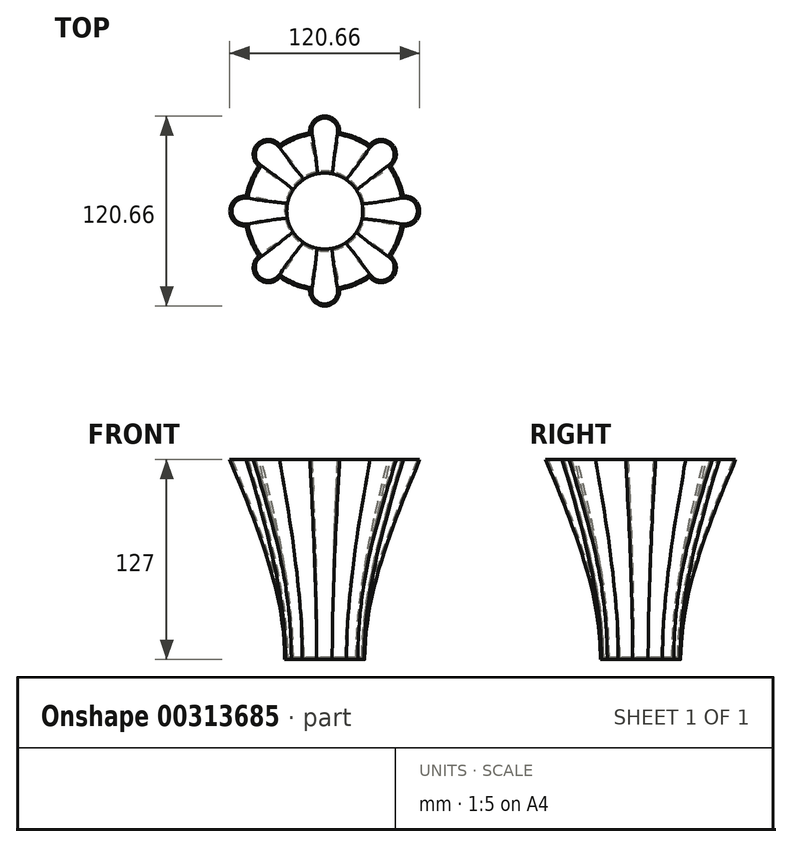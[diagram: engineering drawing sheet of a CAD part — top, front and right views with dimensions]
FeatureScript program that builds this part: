
annotation { "Feature Type Name" : "Feature", "Feature Type Description" : "" }
export const myFeature = defineFeature(function(context is Context, id is Id, definition is map)
    precondition{}
    {
        {
            var Q0;
            Q0=qCreatedBy(makeId("Top.planeOp"),FACE);
            var sketch = newSketch(context, id + "F0", { "sketchPlane" : qUnion([Q0])});
            skCircle(sketch, "E0", {"center": v(0, 0) * mm, "radius": 25.4 * mm});
            skPoint(sketch, "E1", {"position": v(-25.4, 0) * mm});
            skSolve(sketch);
        }
        {
            var Q0;
            Q0=qCreatedBy(makeId("Top.planeOp"),FACE);
            cPlane(context, id + "F1", {"entities" : qUnion([Q0]), "cplaneType" : CPlaneType.OFFSET, "offset" : 127 * mm, "width" : 152.4 * mm, "height" : 152.4 * mm});
        }
        {
            var Q0;
            Q0=qCreatedBy(id+"F1.planeOp",FACE);
            var sketch = newSketch(context, id + "F2", { "sketchPlane" : qUnion([Q0])});
            skArc(sketch, "E2", {"start": v(-42, 28.58) * mm, "mid": v(-46.93, 19.44) * mm, "end": v(-49.9, 9.48) * mm});
            skArc(sketch, "E3", {"start": v(49.9, -9.48) * mm, "mid": v(60.33, 0) * mm, "end": v(49.9, 9.48) * mm});
            skArc(sketch, "E4.1.0", {"start": v(42, 28.58) * mm, "mid": v(42.66, 42.66) * mm, "end": v(28.58, 42) * mm});
            skArc(sketch, "E4.2.0", {"start": v(9.48, 49.9) * mm, "mid": v(0, 60.33) * mm, "end": v(-9.48, 49.9) * mm});
            skArc(sketch, "E5.2.3.0", {"start": v(-28.58, 42) * mm, "mid": v(-42.66, 42.66) * mm, "end": v(-42, 28.58) * mm});
            skArc(sketch, "E5.2.4.0", {"start": v(-49.9, 9.48) * mm, "mid": v(-60.33, 0) * mm, "end": v(-49.9, -9.48) * mm});
            skArc(sketch, "E5.2.5.0", {"start": v(-42, -28.58) * mm, "mid": v(-42.66, -42.66) * mm, "end": v(-28.58, -42) * mm});
            skArc(sketch, "E5.2.6.0", {"start": v(-9.48, -49.9) * mm, "mid": v(0, -60.33) * mm, "end": v(9.48, -49.9) * mm});
            skArc(sketch, "E5.2.7.0", {"start": v(28.58, -42) * mm, "mid": v(42.66, -42.66) * mm, "end": v(42, -28.58) * mm});
            skArc(sketch, "E6.trimOffspring", {"start": v(-49.9, -9.48) * mm, "mid": v(-46.93, -19.44) * mm, "end": v(-42, -28.58) * mm});
            skArc(sketch, "E7.trimOffspring", {"start": v(-9.48, 49.9) * mm, "mid": v(-19.44, 46.93) * mm, "end": v(-28.58, 42) * mm});
            skArc(sketch, "E8.trimOffspring", {"start": v(28.58, 42) * mm, "mid": v(19.44, 46.93) * mm, "end": v(9.48, 49.9) * mm});
            skArc(sketch, "E9.trimOffspring", {"start": v(49.9, 9.48) * mm, "mid": v(46.93, 19.44) * mm, "end": v(42, 28.58) * mm});
            skArc(sketch, "E10.trimOffspring", {"start": v(42, -28.58) * mm, "mid": v(46.93, -19.44) * mm, "end": v(49.9, -9.48) * mm});
            skArc(sketch, "E11.trimOffspring", {"start": v(9.48, -49.9) * mm, "mid": v(19.44, -46.93) * mm, "end": v(28.58, -42) * mm});
            skArc(sketch, "E12.trimOffspring", {"start": v(-28.58, -42) * mm, "mid": v(-19.44, -46.93) * mm, "end": v(-9.48, -49.9) * mm});
            skSolve(sketch);
        }
        {
            var Q0;
            Q0=makeQuery(id+"F0.imprint","IMPRINT",FACE,{"disambiguationData":[TD([[makeQuery(id+"F0.imprint","IMPRINT",EDGE,{"derivedFrom":sQuery(id+"F0.wireOp",EDGE,"E0")}),1.0]])]});
            var Q1;
            Q1=makeQuery(id+"F2.imprint","IMPRINT",FACE,{"disambiguationData":[TD([[makeQuery(id+"F2.imprint","IMPRINT",EDGE,{"derivedFrom":sQuery(id+"F2.wireOp",EDGE,"E2")}),1.0]])]});
            loft(context, id + "F3", {"startCondition" : LoftEndDerivativeType.NORMAL_TO_PROFILE, "startMagnitude" : 1, "sheetProfilesArray" : [{ "sheetProfileEntities" : qUnion([Q0]) }, { "sheetProfileEntities" : qUnion([Q1]) }]});
        }
        {
            var Q0;
            Q0=makeQuery(id+"F3.opLoft","CAP_FACE",FACE,{"disambiguationData":[OSD([makeQuery(id+"F2.imprint","IMPRINT",FACE,{"disambiguationData":[TD([[makeQuery(id+"F2.imprint","IMPRINT",EDGE,{"derivedFrom":sQuery(id+"F2.wireOp",EDGE,"E2")}),1.0]])]})])],"isStart":true});
            var Q1;
            Q1=makeQuery(id+"F3.opLoft","SWEPT_BODY",BODY,{"disambiguationData":[OSD([makeQuery(id+"F0.imprint","IMPRINT",FACE,{"disambiguationData":[TD([[makeQuery(id+"F0.imprint","IMPRINT",EDGE,{"derivedFrom":sQuery(id+"F0.wireOp",EDGE,"E0")}),1.0]])]}),makeQuery(id+"F2.imprint","IMPRINT",FACE,{"disambiguationData":[TD([[makeQuery(id+"F2.imprint","IMPRINT",EDGE,{"derivedFrom":sQuery(id+"F2.wireOp",EDGE,"E2")}),1.0]])]})])]});
            shell(context, id + "F4", {"entities" : qUnion([Q0]), "parts" : qUnion([Q1]), "thickness" : 1.27 * mm});
        }
    });
